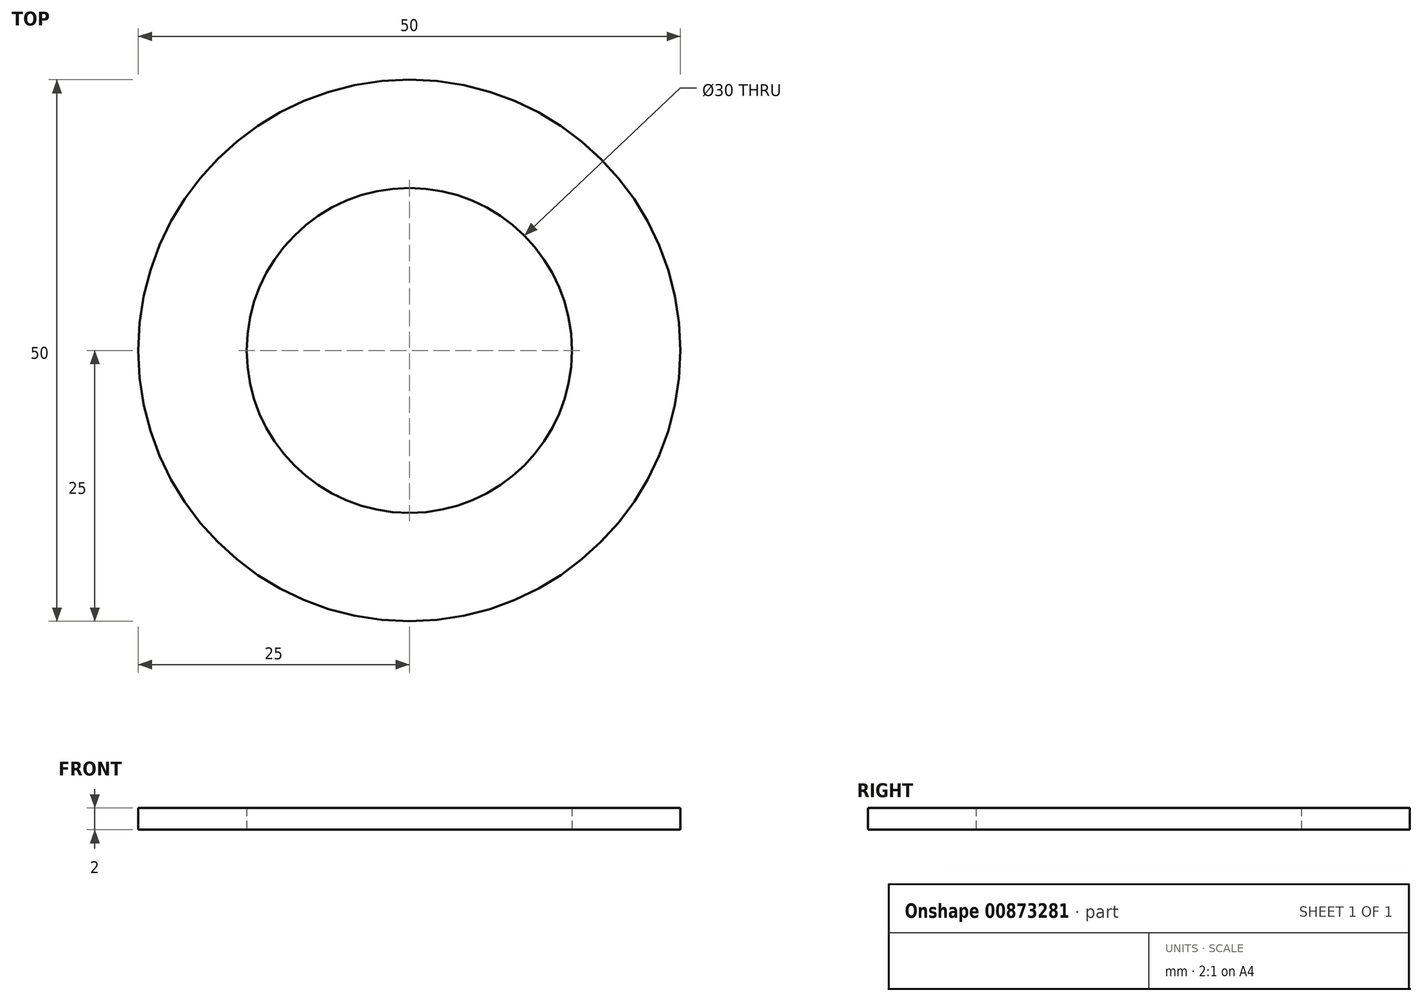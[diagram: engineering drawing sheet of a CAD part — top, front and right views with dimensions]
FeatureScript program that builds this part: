
annotation { "Feature Type Name" : "Feature", "Feature Type Description" : "" }
export const myFeature = defineFeature(function(context is Context, id is Id, definition is map)
    precondition{}
    {
        {
            var Q0;
            Q0=qCreatedBy(makeId("Top.planeOp"),FACE);
            var sketch = newSketch(context, id + "F0", { "sketchPlane" : qUnion([Q0])});
            skCircle(sketch, "E0", {"center": v(0, 0) * mm, "radius": 25 * mm});
            skCircle(sketch, "E1", {"center": v(0, 0) * mm, "radius": 15 * mm});
            skSolve(sketch);
        }
        {
            var Q0;
            Q0=makeQuery(id+"F0.imprint","IMPRINT",FACE,{"disambiguationData":[TD([[makeQuery(id+"F0.imprint","IMPRINT",EDGE,{"derivedFrom":sQuery(id+"F0.wireOp",EDGE,"E0")}),1.0]])]});
            extrude(context, id + "F1", {"entities" : qUnion([Q0]), "depth" : 2 * mm, "offsetDistance" : 25 * mm});
        }
    });
